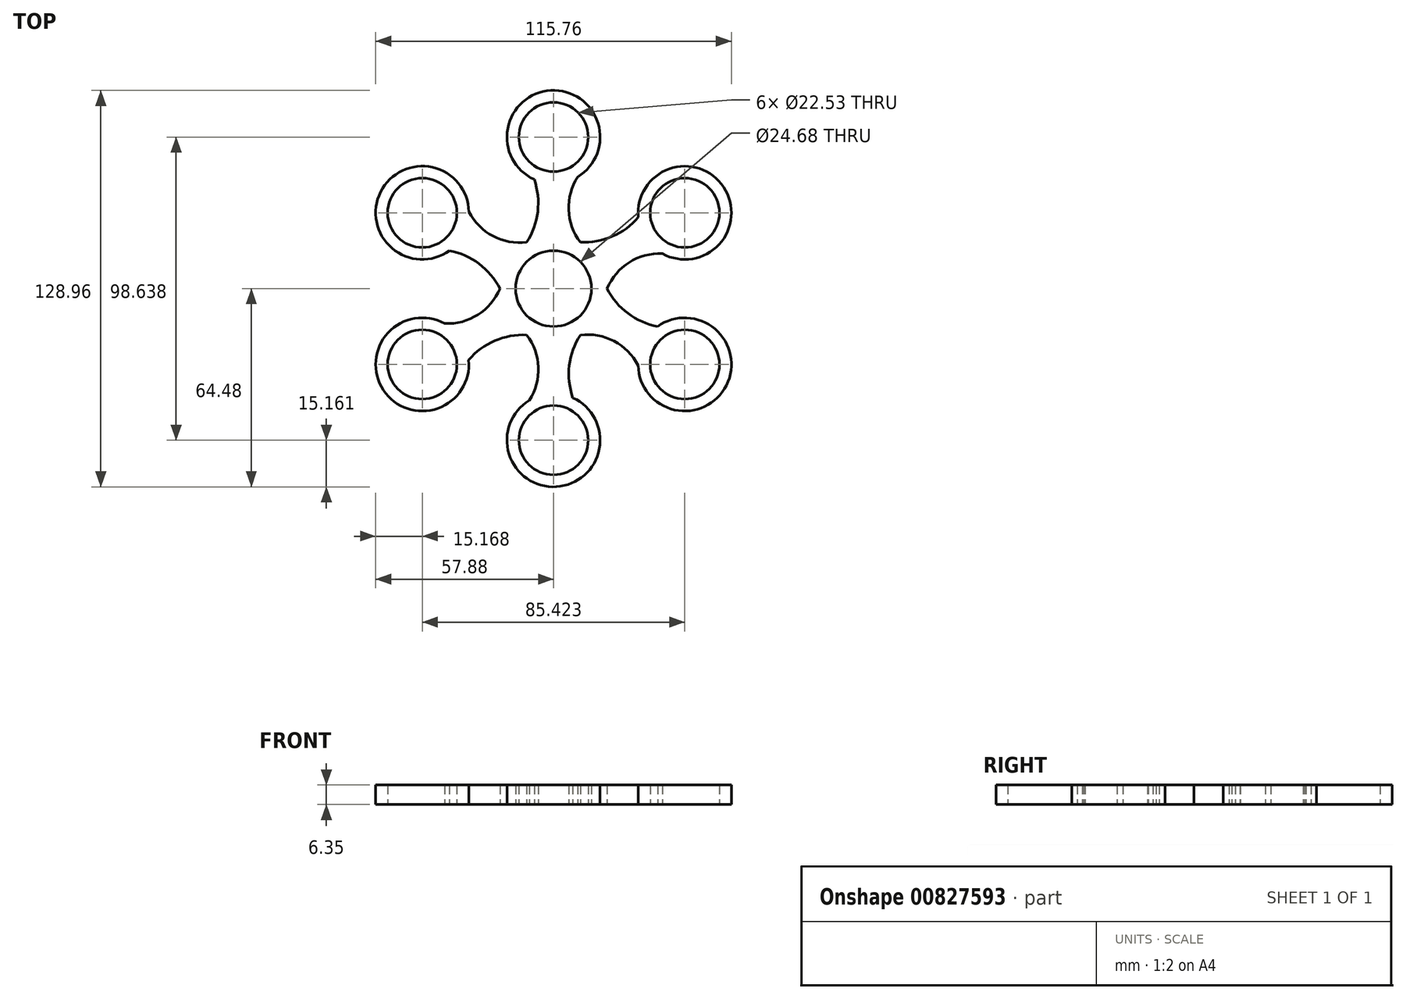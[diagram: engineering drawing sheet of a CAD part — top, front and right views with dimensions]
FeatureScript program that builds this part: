
annotation { "Feature Type Name" : "Feature", "Feature Type Description" : "" }
export const myFeature = defineFeature(function(context is Context, id is Id, definition is map)
    precondition{}
    {
        {
            var Q0;
            Q0=qCreatedBy(makeId("Top.planeOp"),FACE);
            var sketch = newSketch(context, id + "F0", { "sketchPlane" : qUnion([Q0])});
            skCircle(sketch, "E0", {"center": v(0, 0) * mm, "radius": 12.34 * mm});
            skCircle(sketch, "E1", {"center": v(0, 49.32) * mm, "radius": 11.27 * mm});
            skArc(sketch, "E2", {"start": v(7.87, 36.36) * mm, "mid": v(-0.9, 64.46) * mm, "end": v(-6.28, 35.52) * mm});
            skArc(sketch, "E3", {"start": v(-17.27, 0.38) * mm, "mid": v(-17.28, 0.04) * mm, "end": v(-17.27, -0.3) * mm});
            skArc(sketch, "E4", {"start": v(7.87, 36.36) * mm, "mid": v(4.95, 25.39) * mm, "end": v(8.96, 14.77) * mm});
            skArc(sketch, "E5", {"start": v(-8.9, 14.8) * mm, "mid": v(-5.15, 24.85) * mm, "end": v(-6.28, 35.52) * mm});
            skCircle(sketch, "E6.1.0", {"center": v(-42.71, 24.66) * mm, "radius": 11.27 * mm});
            skArc(sketch, "E6.1.1", {"start": v(-27.55, 25) * mm, "mid": v(-56.27, 31.45) * mm, "end": v(-33.9, 12.32) * mm});
            skArc(sketch, "E6.1.2", {"start": v(-17.27, -0.3) * mm, "mid": v(-24.1, 7.96) * mm, "end": v(-33.9, 12.32) * mm});
            skArc(sketch, "E6.1.3", {"start": v(-27.55, 25) * mm, "mid": v(-19.51, 16.98) * mm, "end": v(-8.31, 15.15) * mm});
            skCircle(sketch, "E6.2.0", {"center": v(-42.71, -24.66) * mm, "radius": 11.27 * mm});
            skArc(sketch, "E6.2.1", {"start": v(-35.42, -11.36) * mm, "mid": v(-55.37, -33) * mm, "end": v(-27.62, -23.2) * mm});
            skArc(sketch, "E6.2.2", {"start": v(-8.38, -15.1) * mm, "mid": v(-18.95, -16.9) * mm, "end": v(-27.62, -23.2) * mm});
            skArc(sketch, "E6.2.3", {"start": v(-35.42, -11.36) * mm, "mid": v(-24.46, -8.4) * mm, "end": v(-17.27, 0.38) * mm});
            skCircle(sketch, "E7.1.3.0", {"center": v(0, -49.32) * mm, "radius": 11.27 * mm});
            skArc(sketch, "E7.2.3.0", {"start": v(-7.87, -36.36) * mm, "mid": v(0.9, -64.46) * mm, "end": v(6.28, -35.52) * mm});
            skArc(sketch, "E7.6.3.0", {"start": v(8.9, -14.8) * mm, "mid": v(5.15, -24.85) * mm, "end": v(6.28, -35.52) * mm});
            skArc(sketch, "E7.10.3.0", {"start": v(-7.87, -36.36) * mm, "mid": v(-4.95, -25.39) * mm, "end": v(-8.96, -14.77) * mm});
            skCircle(sketch, "E7.1.4.0", {"center": v(42.71, -24.66) * mm, "radius": 11.27 * mm});
            skArc(sketch, "E7.2.4.0", {"start": v(27.55, -25) * mm, "mid": v(56.27, -31.45) * mm, "end": v(33.9, -12.32) * mm});
            skArc(sketch, "E7.6.4.0", {"start": v(17.27, 0.3) * mm, "mid": v(24.1, -7.96) * mm, "end": v(33.9, -12.32) * mm});
            skArc(sketch, "E7.10.4.0", {"start": v(27.55, -25) * mm, "mid": v(19.51, -16.98) * mm, "end": v(8.31, -15.15) * mm});
            skCircle(sketch, "E7.1.5.0", {"center": v(42.71, 24.66) * mm, "radius": 11.27 * mm});
            skArc(sketch, "E7.2.5.0", {"start": v(35.42, 11.36) * mm, "mid": v(55.37, 33) * mm, "end": v(27.62, 23.2) * mm});
            skArc(sketch, "E7.6.5.0", {"start": v(8.38, 15.1) * mm, "mid": v(18.95, 16.9) * mm, "end": v(27.62, 23.2) * mm});
            skArc(sketch, "E7.10.5.0", {"start": v(35.42, 11.36) * mm, "mid": v(24.46, 8.4) * mm, "end": v(17.27, -0.38) * mm});
            skArc(sketch, "E8.trimOffspring", {"start": v(8.31, -15.15) * mm, "mid": v(8.6, -14.98) * mm, "end": v(8.9, -14.8) * mm});
            skArc(sketch, "E9.trimOffspring", {"start": v(-8.96, -14.77) * mm, "mid": v(-8.67, -14.94) * mm, "end": v(-8.38, -15.1) * mm});
            skArc(sketch, "E10.trimOffspring", {"start": v(17.27, -0.38) * mm, "mid": v(17.28, -0.04) * mm, "end": v(17.27, 0.3) * mm});
            skSolve(sketch);
        }
        {
            var Q0;
            Q0 = qSketchRegion(id + "F0", true);
            extrude(context, id + "F1", {"entities" : qUnion([Q0]), "depth" : 6.35 * mm, "offsetDistance" : 25.4 * mm});
        }
    });
